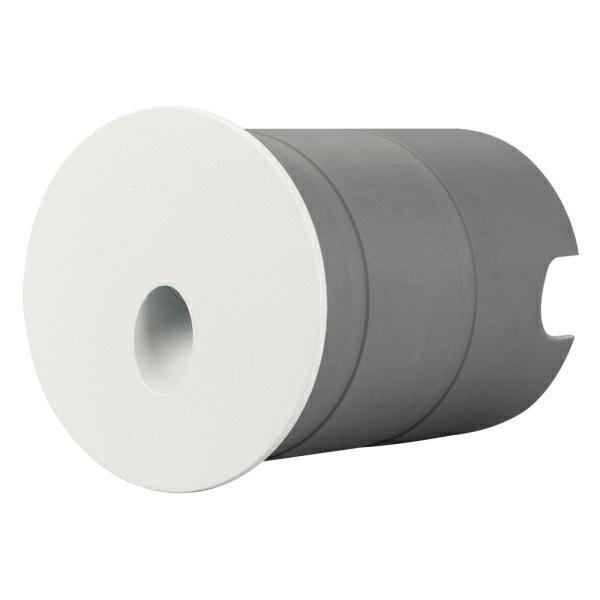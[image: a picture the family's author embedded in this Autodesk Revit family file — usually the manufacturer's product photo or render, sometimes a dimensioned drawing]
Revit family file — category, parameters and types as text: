
# Revit family: GAP
name_source: partatom
category: Осветительные приборы
revit_build: Autodesk Revit 2017 (Build: 20160225_1515(x64)
units: mm (PartAtom-declared; Revit-internal decimal feet)

## family parameters
Источник света = Да
Общий = Нет
Основа = Грань
При загрузке вырезать с полостями = Нет
Размер круглого соединителя = Использовать диаметр
Тип детали = Нормальный
Точка расчета площади = Нет

## types (4) — shared parameters
ADSK_Единица измерения = шт.
ADSK_Завод-изготовитель = ARLIGHT
ADSK_Классификация нагрузок = Освещение
ADSK_Количество фаз = 1
ADSK_Количество фаз числовое = 1
ADSK_Коэффициент мощности = 0.5
ADSK_Наименование = Светильник
ADSK_Напряжение = 230 В
ADSK_Номинальная мощность = 3 Вт
ADSK_Полная мощность = 6 В·А
ADSK_Размер_Высота = 97 мм
ADSK_Размер_Длина = 70 мм
ADSK_Размер_Ширина = 70 мм
ADSK_Ток = 0 А
ARL_Драйвер = Выносной несъемный
ARL_Индекс цветопередачи = >80
ARL_Класс защиты от поражения электрическим током = I
ARL_Класс пылевлагозащиты = IP65
ARL_Область использования = Для локального освещения лестниц, стен, проходов, для применения в интерьерном и архитектурном освещении
ARL_Рабочая температура окружающей среды = -40...+60 °C
ARL_Серия = GAP
ARL_Способ монтажа = Встраиваемый
ARL_Тип товара = Светильник
ARL_Угол обзора = 30°
ARL_Цвет свечения = Теплый 3000К
URL = https://arlight.ru
Видимая форма излучения при визуализации = Нет
Группа модели = Светильники
Изготовитель = ARLIGHT
Изготовитель (сайт) = www.arlight.ru
Изготовитель (телефон) = 8 800 505 26 29
Излучение по диаметру окружности = 10 мм
Отметка по умолчанию = 1219 мм
Полная установленная мощность = 6 В·А
Разработчик = НТЦ Конструктор
Разработчик (URL) = https://constructor.ru
Разработчик (телефон) = +7 (495) 781-05-35
Светофильтр = 16777215
Смещение цветовой температуры при затухании лампы = <Нет>
Угол наклона = 90.00°

## per-type parameters (varying)
| type | ADSK_Код изделия | ADSK_Марка | ADSK_Масса_Текст | ARL_Материал корпуса | ARL_Обозначение корпуса | ARL_Цвет покрытия | Квадратный | Комментарии к типоразмеру | Круглый | Описание | Файл фотометрической сетки |
| 025737 Светильник LT-GAP-R70-3W Warm3000 (WH, 30 deg) | Арт. 025737 | LT-GAP-R70-3W Warm3000 | 0.371 | Металл, белый | Корпус круглый, алюминий, цвет белый | Белый | Нет | Арт. 025737 | Да | Светодиодный встраиваемый круглый светильник для стен, лестниц, 3 Вт. Цвет ТЕПЛЫЙ 3000К, световой поток 120лм, угол 30°, CRI>80. Влагозащищенный корпус IP65, белый алюминий. Питание AC230V, мощность 3 Вт. Размеры DxH 70x97 мм (закладная часть Ø62x95 мм) | 025737_LT-GAP-R70-3W Warm3000 (WH, 30 deg).ies |
| 025738 Светильник LT-GAP-S70x70-3W Warm3000 (WH, 30 deg) | Арт. 025738 | LT-GAP-S70x70-3W Warm3000 | 0.387 | Металл, белый | Корпус квадратный, алюминий, цвет белый | Белый | Да | Арт. 025738 | Нет | Светодиодный встраиваемый квадратный светильник для стен, лестниц, 3 Вт. Цвет ТЕПЛЫЙ 3000К, световой поток 121лм, угол 30°, CRI>80. Влагозащищенный корпус IP65, белый алюминий. Питание AC230V, мощность 3 Вт. Размеры LxWxH 70x70x97 мм (закладная часть Ø62x95 мм) | 025738_ LT-GAP-S70x70-3W Warm3000 (WH, 30 deg).ies |
| 031166 Светильник LT-GAP-R70-3W Warm3000 (BK, 30deg, 230V) | Арт. 031166 | LT-GAP-R70-3W Warm3000 | 0.371 | Металл, чёрный | Корпус круглый, алюминий, цвет черный | Черный | Нет | Арт. 031166 | Да | Светодиодный встраиваемый круглый светильник для стен, лестниц, 3 Вт. Цвет ТЕПЛЫЙ 3000К, световой поток 120лм, угол 30°, CRI>80. Влагозащищенный корпус IP65, черный алюминий. Питание AC230V, мощность 3 Вт. Размеры DxH 70x97 мм (закладная часть Ø62x95 мм) | 031166_ LT-GAP-R70-3W Warm3000 (BK, 30deg, 230V).ies |
| 031167 Светильник LT-GAP-S70x70-3W Warm3000 (BK, 30deg, 230V) | Арт. 031167 | LT-GAP-S70x70-3W Warm3000 | 0.387 | Металл, чёрный | Корпус квадратный, алюминий, цвет черный | Черный | Да | Арт. 031167 | Нет | Светодиодный встраиваемый квадратный светильник для стен, лестниц, 3 Вт. Цвет ТЕПЛЫЙ 3000К, световой поток 121лм, угол 30°, CRI>80. Влагозащищенный корпус IP65, черный алюминий. Питание AC230V, мощность 3 Вт. Размеры LxWxH 70x70x97 мм (закладная часть Ø62x95 мм) | 031167_LT-GAP-S70x70-3W Warm3000 (BK, 30deg, 230V).ies |
